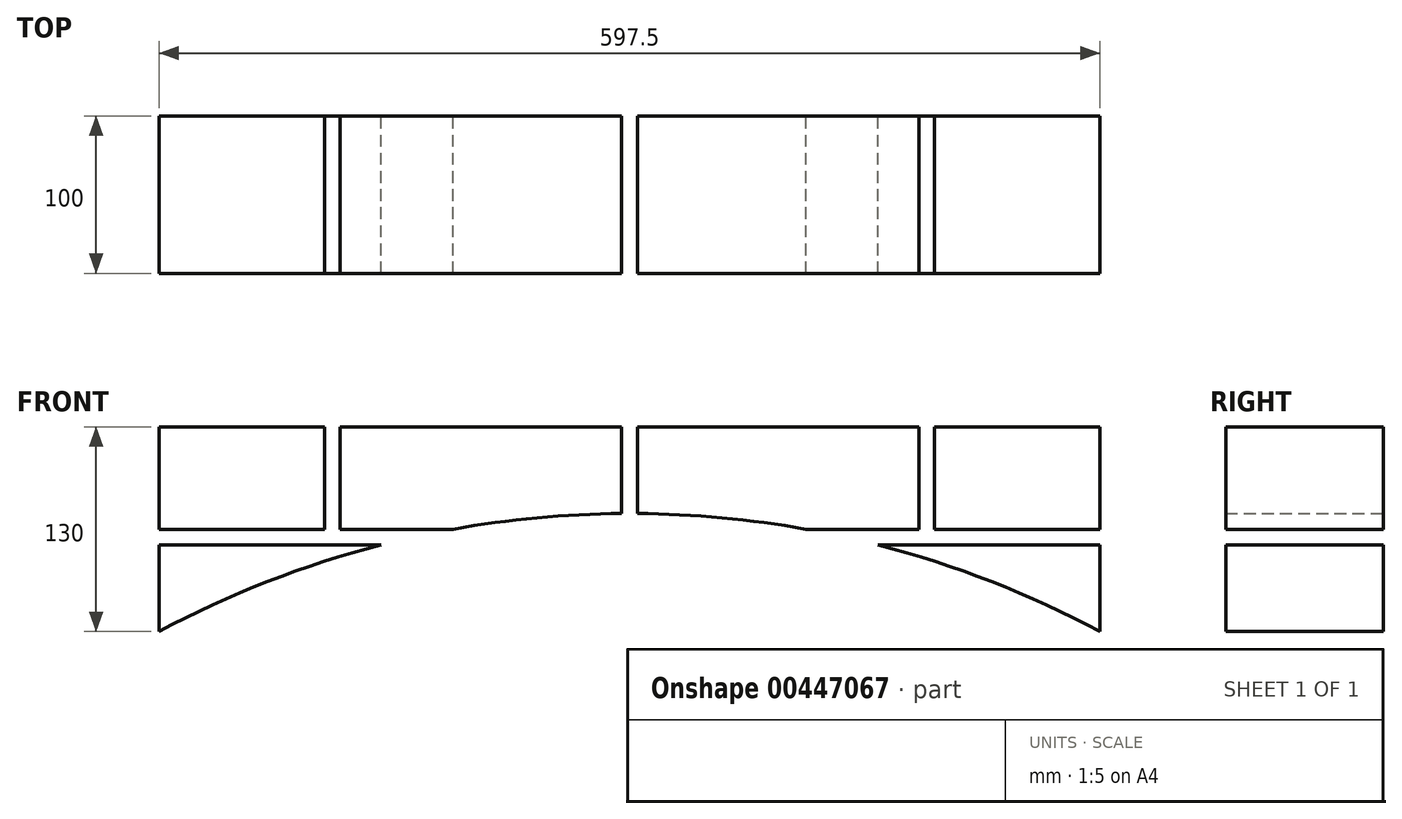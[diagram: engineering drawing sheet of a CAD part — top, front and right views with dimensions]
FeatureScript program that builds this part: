
annotation { "Feature Type Name" : "Feature", "Feature Type Description" : "" }
export const myFeature = defineFeature(function(context is Context, id is Id, definition is map)
    precondition{}
    {
        {
            var Q0;
            Q0=qCreatedBy(makeId("Front.planeOp"),FACE);
            var sketch = newSketch(context, id + "F0", { "sketchPlane" : qUnion([Q0])});
            skLineSegment(sketch, "E0.bottom", {"start": v(0, 0) * mm, "end": v(597.5, 0) * mm, "construction": true});
            skLineSegment(sketch, "E0.top", {"start": v(0, 215) * mm, "end": v(597.5, 215) * mm, "construction": true});
            skLineSegment(sketch, "E0.left", {"start": v(0, 0) * mm, "end": v(0, 215) * mm, "construction": true});
            skLineSegment(sketch, "E0.right", {"start": v(597.5, 0) * mm, "end": v(597.5, 215) * mm, "construction": true});
            skLineSegment(sketch, "E1", {"start": v(0, 75) * mm, "end": v(597.5, 75) * mm, "construction": true});
            skLineSegment(sketch, "E2", {"start": v(298.75, 0) * mm, "end": v(298.75, 215) * mm, "construction": true});
            skLineSegment(sketch, "E3", {"start": v(298.75, 0) * mm, "end": v(298.75, -557.51) * mm, "construction": true});
            skArc(sketch, "E4", {"start": v(0, 0) * mm, "mid": v(298.75, 75) * mm, "end": v(597.5, 0) * mm});
            skPoint(sketch, "E5", {"position": v(298.75, 75) * mm});
            skArc(sketch, "E6", {"start": v(0, 75) * mm, "mid": v(298.75, 150) * mm, "end": v(597.5, 75) * mm});
            skArc(sketch, "E7", {"start": v(0, 85) * mm, "mid": v(298.75, 160) * mm, "end": v(597.5, 85) * mm});
            skLineSegment(sketch, "E8", {"start": v(0, 85) * mm, "end": v(0, 0) * mm});
            skLineSegment(sketch, "E9", {"start": v(597.5, 85) * mm, "end": v(597.5, 0) * mm});
            skLineSegment(sketch, "E10", {"start": v(0, 215) * mm, "end": v(0, 150) * mm});
            skLineSegment(sketch, "E11", {"start": v(0, 150) * mm, "end": v(186.72, 150) * mm});
            skLineSegment(sketch, "E12", {"start": v(0, 215) * mm, "end": v(597.5, 215) * mm});
            skLineSegment(sketch, "E13", {"start": v(0, 150) * mm, "end": v(0, 85) * mm});
            skLineSegment(sketch, "E14", {"start": v(0, 140) * mm, "end": v(140.95, 140) * mm});
            skLineSegment(sketch, "E15", {"start": v(105, 150) * mm, "end": v(105, 215) * mm});
            skLineSegment(sketch, "E16", {"start": v(115, 215) * mm, "end": v(115, 150) * mm});
            skLineSegment(sketch, "E17", {"start": v(293.75, 159.98) * mm, "end": v(293.75, 215) * mm});
            skLineSegment(sketch, "E18", {"start": v(597.5, 215) * mm, "end": v(597.5, 85) * mm});
            skLineSegment(sketch, "E19", {"start": v(456.55, 140) * mm, "end": v(597.5, 140) * mm});
            skLineSegment(sketch, "E20", {"start": v(597.5, 150) * mm, "end": v(410.78, 150) * mm});
            skLineSegment(sketch, "E21", {"start": v(492.5, 150) * mm, "end": v(492.5, 215) * mm});
            skLineSegment(sketch, "E22", {"start": v(482.5, 150) * mm, "end": v(482.5, 215) * mm});
            skLineSegment(sketch, "E23", {"start": v(303.75, 215) * mm, "end": v(303.75, 159.98) * mm});
            skSolve(sketch);
        }
        {
            var Q0;
            {var subQ0=sQuery(id+"F0.wireOp",EDGE,"E10");Q0=makeQuery(id+"F0.imprint","IMPRINT",FACE,{"disambiguationData":[TD([[makeQuery(id+"F0.imprint","IMPRINT",EDGE,{"derivedFrom":subQ0}),1.0]])]});}
            var Q1;
            {var subQ0=sQuery(id+"F0.wireOp",EDGE,"E16");Q1=makeQuery(id+"F0.imprint","IMPRINT",FACE,{"disambiguationData":[TD([[makeQuery(id+"F0.imprint","IMPRINT",EDGE,{"derivedFrom":subQ0}),1.0]])]});}
            var Q2;
            {var subQ0=sQuery(id+"F0.wireOp",EDGE,"E22");Q2=makeQuery(id+"F0.imprint","IMPRINT",FACE,{"disambiguationData":[TD([[makeQuery(id+"F0.imprint","IMPRINT",EDGE,{"derivedFrom":subQ0}),1.0]])]});}
            var Q3;
            {var subQ3=sQuery(id+"F0.wireOp",EDGE,"E21");Q3=makeQuery(id+"F0.imprint","IMPRINT",FACE,{"disambiguationData":[TD([[makeQuery(id+"F0.imprint","IMPRINT",EDGE,{"derivedFrom":subQ3}),-1.0]])]});}
            var Q4;
            {var subQ3=sQuery(id+"F0.wireOp",EDGE,"E19");Q4=makeQuery(id+"F0.imprint","IMPRINT",FACE,{"disambiguationData":[TD([[makeQuery(id+"F0.imprint","IMPRINT",EDGE,{"derivedFrom":subQ3}),-1.0]])]});}
            var Q5;
            {var subQ0=sQuery(id+"F0.wireOp",EDGE,"E4");Q5=makeQuery(id+"F0.imprint","IMPRINT",FACE,{"disambiguationData":[TD([[makeQuery(id+"F0.imprint","IMPRINT",EDGE,{"derivedFrom":subQ0}),1.0]])]});}
            var Q6;
            {var subQ3=sQuery(id+"F0.wireOp",EDGE,"E14");Q6=makeQuery(id+"F0.imprint","IMPRINT",FACE,{"disambiguationData":[TD([[makeQuery(id+"F0.imprint","IMPRINT",EDGE,{"derivedFrom":subQ3}),-1.0]])]});}
            extrude(context, id + "F1", {"entities" : qUnion([Q0, Q1, Q2, Q3, Q4, Q5, Q6]), "depth" : 100 * mm, "offsetDistance" : 25 * mm});
        }
    });
